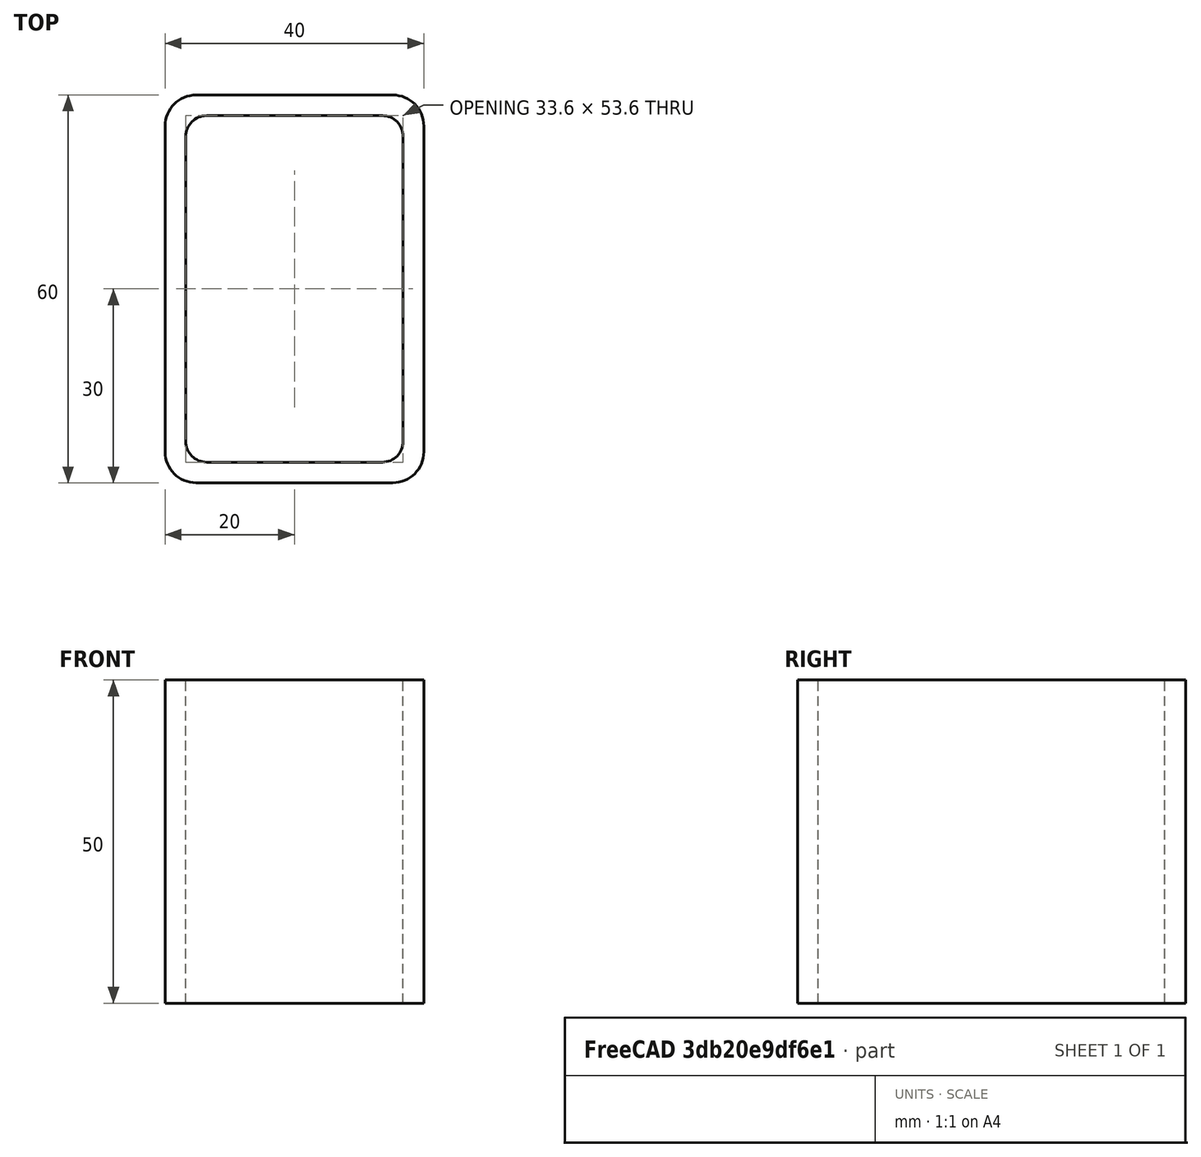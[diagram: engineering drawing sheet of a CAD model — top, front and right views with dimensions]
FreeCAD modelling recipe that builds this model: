
FCSTD DOCUMENT  (FreeCAD 0.15R4671 (Git))
Label: Rectangular hollow section 60x40x3.2 EN10219 S235JRH
License: All rights reserved
LicenseURL: http://en.wikipedia.org/wiki/All_rights_reserved
objects: Sketcher::SketchObject×1, Part::Extrusion×1
note: 2 computed .brp shape members not serialized (recipe doc carries the construction recipe); baked Part::Feature solids carry a one-line shape summary decoded from their .brp

FEATURE [Sketcher::SketchObject] Sketch
  sketch-geometry (16):
    g0: LineSegment StartX=-13.6 StartY=26.8 StartZ=0 EndX=13.6 EndY=26.8 EndZ=0
    g1: LineSegment StartX=16.8 StartY=23.6 StartZ=0 EndX=16.8 EndY=-23.6 EndZ=0
    g2: LineSegment StartX=13.6 StartY=-26.8 StartZ=0 EndX=-13.6 EndY=-26.8 EndZ=0
    g3: LineSegment StartX=-16.8 StartY=-23.6 StartZ=0 EndX=-16.8 EndY=23.6 EndZ=0
    g4: LineSegment StartX=-15.2 StartY=30 StartZ=0 EndX=15.2 EndY=30 EndZ=0
    g5: LineSegment StartX=20 StartY=25.2 StartZ=0 EndX=20 EndY=-25.2 EndZ=0
    g6: LineSegment StartX=15.2 StartY=-30 StartZ=0 EndX=-15.2 EndY=-30 EndZ=0
    g7: LineSegment StartX=-20 StartY=-25.2 StartZ=0 EndX=-20 EndY=25.2 EndZ=0
    g8: ArcOfCircle CenterX=-13.6 CenterY=23.6 CenterZ=0 NormalX=0 NormalY=0 NormalZ=1 Radius=3.2 StartAngle=1.5708 EndAngle=3.14159
    g9: ArcOfCircle CenterX=13.6 CenterY=23.6 CenterZ=0 NormalX=0 NormalY=0 NormalZ=1 Radius=3.2 StartAngle=0 EndAngle=1.5708
    g10: ArcOfCircle CenterX=13.6 CenterY=-23.6 CenterZ=0 NormalX=0 NormalY=0 NormalZ=1 Radius=3.2 StartAngle=4.71239 EndAngle=6.28319
    g11: ArcOfCircle CenterX=-13.6 CenterY=-23.6 CenterZ=0 NormalX=0 NormalY=0 NormalZ=1 Radius=3.2 StartAngle=3.14159 EndAngle=4.71239
    g12: ArcOfCircle CenterX=15.2 CenterY=25.2 CenterZ=0 NormalX=0 NormalY=0 NormalZ=1 Radius=4.8 StartAngle=0 EndAngle=1.5708
    g13: ArcOfCircle CenterX=15.2 CenterY=-25.2 CenterZ=0 NormalX=0 NormalY=0 NormalZ=1 Radius=4.8 StartAngle=4.71239 EndAngle=6.28319
    g14: ArcOfCircle CenterX=-15.2 CenterY=-25.2 CenterZ=0 NormalX=0 NormalY=0 NormalZ=1 Radius=4.8 StartAngle=3.14159 EndAngle=4.71239
    g15: ArcOfCircle CenterX=-15.2 CenterY=25.2 CenterZ=0 NormalX=0 NormalY=0 NormalZ=1 Radius=4.8 StartAngle=1.5708 EndAngle=3.14159
  constraints (36):
    c: Horizontal(g2)
    c: Vertical(g3)
    c: Horizontal(g6)
    c: Vertical(g7)
    c: Tangent(g3,g8) = 1.5708
    c: Tangent(g0,g8) = 1.5708
    c: Tangent(g0,g9) = 1.5708
    c: Tangent(g1,g9) = 1.5708
    c: Tangent(g1,g10) = 1.5708
    c: Tangent(g2,g10) = 1.5708
    c: Tangent(g2,g11) = 1.5708
    c: Tangent(g3,g11) = 1.5708
    c: Tangent(g4,g12) = 1.5708
    c: Tangent(g5,g12) = 1.5708
    c: Tangent(g5,g13) = 1.5708
    c: Tangent(g6,g13) = 1.5708
    c: Tangent(g6,g14) = 1.5708
    c: Tangent(g7,g14) = 1.5708
    c: Tangent(g7,g15) = 1.5708
    c: Tangent(g4,g15) = 1.5708
    c: Equal(g9,g8)
    c: Equal(g9,g11)
    c: Equal(g9,g10)
    c: Equal(g12,g15)
    c: Equal(g12,g14)
    c: Equal(g12,g13)
    c: Symmetric(g4,g6,g-1)
    c: Symmetric(g7,g5,g-2)
    c: DistanceY(g4,g6) = -60
    c: DistanceX(g7,g5) = 40
    c: Symmetric(g3,g1,g-2)
    c: Symmetric(g0,g2,g-1)
    c: DistanceY(g0,g4) = 3.2
    c: DistanceX(g5,g1) = -3.2
    c: Radius(g9) = 3.2
    c: Radius(g12) = 4.8
FEATURE [Part::Extrusion] Extrude  label="Rectangular hollow section 60x40x3.2 EN10219 S235JRH"
  Base = -> Sketch
  Dir = (0,0,50)
  Solid = true
